SOLIDWORKS PART (.sldprt)
format: sldprt  version: not decoded by parser v0  size: 138,240 bytes
history: native  units: mm
features: sketch x5, plane x3, extrude x3, cut_extrude x2, material x1 (+9 scaffold rows collapsed)
feature tree (23):
  scaffold x9  (default folders/planes/origin — collapsed)
  material  "Material <not specified>"
  plane  "Plan de face"
  plane  "Plan de dessus"
  plane  "Plan de droite"
  sketch  "Sketch1"  dims[D1=10.0mm D2=150.0mm D3=75.5mm]
  extrude  "Boss-Extrude1"  Depth=55mm
  sketch  "Sketch2"  dims[D1=10.0mm]
  extrude  "Boss-Extrude2"  Depth=45mm
  sketch  "Sketch3"  dims[D1=45.0mm D2=8.0mm D3=25.0mm]
  extrude  "Boss-Extrude3"  Depth=42mm
  sketch  "Sketch4"
  cut_extrude  "Cut-Extrude1"  [1 undecoded]
  sketch  "Sketch5"  dims[D1=23.0mm]
  cut_extrude  "Cut-Extrude2"  [1 undecoded]
decode coverage: 7 of 10 modeling features carry decoded parameters
note: 2 parameter values undecoded
note: suppression state not decoded; provenance and decode notes live in map.json
